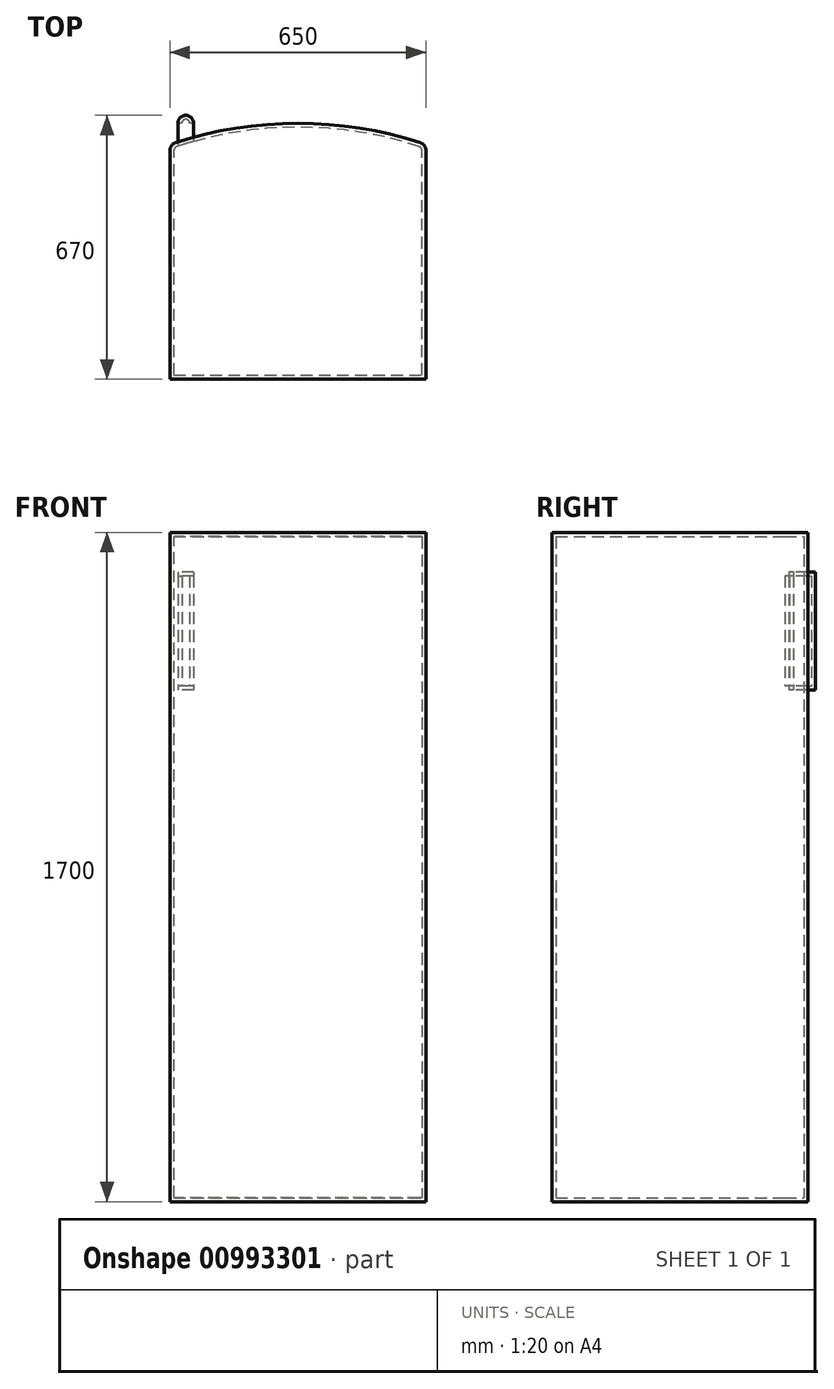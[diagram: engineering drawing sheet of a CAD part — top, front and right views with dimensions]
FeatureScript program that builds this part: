
annotation { "Feature Type Name" : "Feature", "Feature Type Description" : "" }
export const myFeature = defineFeature(function(context is Context, id is Id, definition is map)
    precondition{}
    {
        {
            var Q0;
            Q0=qCreatedBy(makeId("Top.planeOp"),FACE);
            var sketch = newSketch(context, id + "F0", { "sketchPlane" : qUnion([Q0])});
            skLineSegment(sketch, "E0.bottom", {"start": v(0, 0) * mm, "end": v(650, 0) * mm});
            skLineSegment(sketch, "E0.top", {"start": v(0, 650) * mm, "end": v(650, 650) * mm, "construction": true});
            skLineSegment(sketch, "E0.left", {"start": v(0, 0) * mm, "end": v(0, 581.33) * mm});
            skLineSegment(sketch, "E0.right", {"start": v(650, 0) * mm, "end": v(650, 581.33) * mm});
            skArc(sketch, "E1", {"start": v(636.22, 600.34) * mm, "mid": v(325, 650) * mm, "end": v(13.78, 600.34) * mm});
            skPoint(sketch, "E2.visualSharp", {"position": v(0, 595.71) * mm});
            skArc(sketch, "E2.filletArc", {"start": v(13.78, 600.34) * mm, "mid": v(3.8, 593.07) * mm, "end": v(0, 581.33) * mm});
            skPoint(sketch, "E3.visualSharp", {"position": v(650, 595.71) * mm});
            skArc(sketch, "E3.filletArc", {"start": v(650, 581.33) * mm, "mid": v(646.2, 593.07) * mm, "end": v(636.22, 600.34) * mm});
            skSolve(sketch);
        }
        {
            var Q0;
            Q0 = qSketchRegion(id + "F0", true);
            extrude(context, id + "F1", {"entities" : qUnion([Q0]), "depth" : 1700 * mm, "offsetDistance" : 25 * mm});
        }
        {
            var Q0;
            Q0=qCreatedBy(makeId("Top.planeOp"),FACE);
            var sketch = newSketch(context, id + "F2", { "sketchPlane" : qUnion([Q0])});
            skLineSegment(sketch, "E4.bottom", {"start": v(40, 670) * mm, "end": v(40, 670) * mm});
            skLineSegment(sketch, "E4.top", {"start": v(60, 470) * mm, "end": v(20, 470) * mm});
            skLineSegment(sketch, "E4.left", {"start": v(60, 650) * mm, "end": v(60, 470) * mm});
            skLineSegment(sketch, "E4.right", {"start": v(20, 650) * mm, "end": v(20, 470) * mm});
            skPoint(sketch, "E5.visualSharp", {"position": v(60, 670) * mm});
            skArc(sketch, "E5.filletArc", {"start": v(60, 650) * mm, "mid": v(54.14, 664.14) * mm, "end": v(40, 670) * mm});
            skPoint(sketch, "E6.visualSharp", {"position": v(20, 670) * mm});
            skArc(sketch, "E6.filletArc", {"start": v(40, 670) * mm, "mid": v(25.86, 664.14) * mm, "end": v(20, 650) * mm});
            skSolve(sketch);
        }
        {
            var Q0;
            Q0=makeQuery(id+"F2.imprint","IMPRINT",FACE,{"disambiguationData":[TD([[makeQuery(id+"F2.imprint","IMPRINT",EDGE,{"derivedFrom":sQuery(id+"F2.wireOp",EDGE,"E4.top")}),-1.0]])]});
            extrude(context, id + "F3", {"entities" : qUnion([Q0]), "operationType" : NewBodyOperationType.ADD, "depth" : 1600 * mm, "offsetDistance" : 25 * mm, "hasSecondDirection" : true, "secondDirectionOppositeDirection" : false, "secondDirectionDepth" : 1300 * mm});
        }
        {
            var Q0;
            Q0=makeQuery(id+"F3.opExtrude","SWEPT_FACE",FACE,{"disambiguationData":[OSD([sQuery(id+"F2.wireOp",EDGE,"E4.right")])]});
            var Q1;
            Q1=makeQuery(id+"F3.opExtrude","SWEPT_FACE",FACE,{"disambiguationData":[OSD([sQuery(id+"F2.wireOp",EDGE,"E4.left")])]});
            shell(context, id + "F4", {"entities" : qUnion([Q0, Q1]), "thickness" : 10 * mm});
        }
    });
